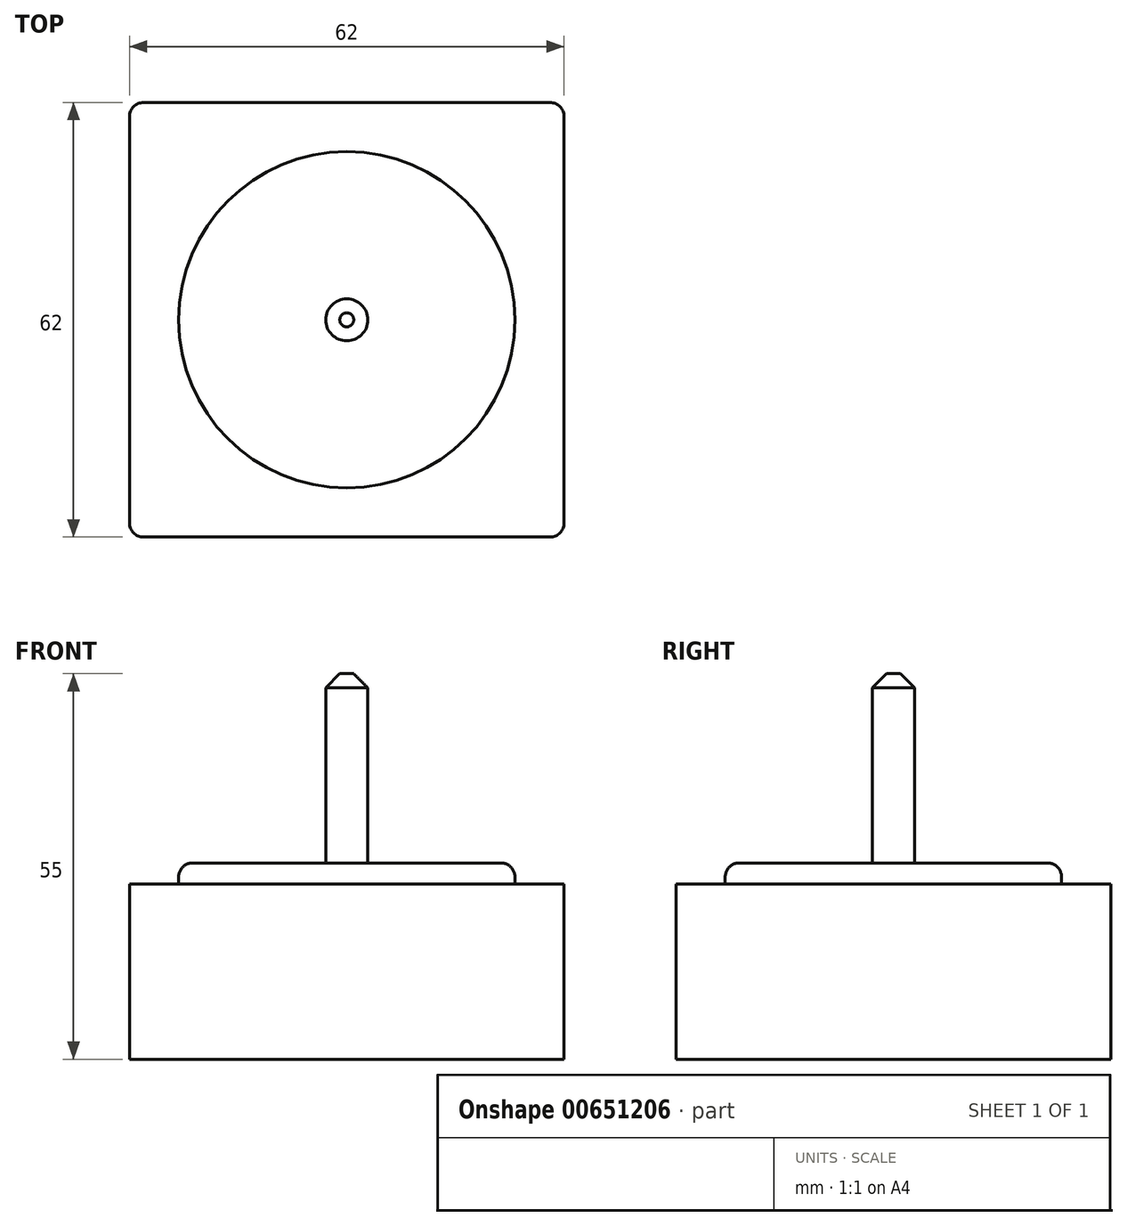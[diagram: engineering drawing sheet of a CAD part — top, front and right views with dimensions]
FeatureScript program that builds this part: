
annotation { "Feature Type Name" : "Feature", "Feature Type Description" : "" }
export const myFeature = defineFeature(function(context is Context, id is Id, definition is map)
    precondition{}
    {
        {
            var Q0;
            Q0=qCreatedBy(makeId("Top.planeOp"),FACE);
            var sketch = newSketch(context, id + "F0", { "sketchPlane" : qUnion([Q0])});
            skLineSegment(sketch, "E0.bottom", {"start": v(-31, 31) * mm, "end": v(31, 31) * mm});
            skLineSegment(sketch, "E0.top", {"start": v(-31, -31) * mm, "end": v(31, -31) * mm});
            skLineSegment(sketch, "E0.left", {"start": v(-31, 31) * mm, "end": v(-31, -31) * mm});
            skLineSegment(sketch, "E0.right", {"start": v(31, 31) * mm, "end": v(31, -31) * mm});
            skPoint(sketch, "E0.middle", {"position": v(0, 0) * mm});
            skCircle(sketch, "E1", {"center": v(0, 0) * mm, "radius": 24 * mm});
            skCircle(sketch, "E2", {"center": v(0, 0) * mm, "radius": 3 * mm});
            skSolve(sketch);
        }
        {
            var Q0;
            Q0=makeQuery(id+"F0.imprint","IMPRINT",FACE,{"disambiguationData":[TD([[makeQuery(id+"F0.imprint","IMPRINT",EDGE,{"derivedFrom":sQuery(id+"F0.wireOp",EDGE,"E1")}),1.0]])]});
            var Q1;
            Q1=makeQuery(id+"F0.imprint","IMPRINT",FACE,{"disambiguationData":[TD([[makeQuery(id+"F0.imprint","IMPRINT",EDGE,{"derivedFrom":sQuery(id+"F0.wireOp",EDGE,"E2")}),1.0]])]});
            extrude(context, id + "F1", {"entities" : qUnion([Q0, Q1]), "depth" : 3 * mm, "offsetDistance" : 25 * mm});
        }
        {
            var Q0;
            Q0=makeQuery(id+"F0.imprint","IMPRINT",FACE,{"disambiguationData":[TD([[makeQuery(id+"F0.imprint","IMPRINT",EDGE,{"derivedFrom":sQuery(id+"F0.wireOp",EDGE,"E2")}),1.0]])]});
            extrude(context, id + "F2", {"entities" : qUnion([Q0]), "operationType" : NewBodyOperationType.ADD, "depth" : 30 * mm, "offsetDistance" : 25 * mm});
        }
        {
            var Q0;
            Q0=makeQuery(id+"F0.imprint","IMPRINT",FACE,{"disambiguationData":[TD([[makeQuery(id+"F0.imprint","IMPRINT",EDGE,{"derivedFrom":sQuery(id+"F0.wireOp",EDGE,"E0.bottom")}),-1.0]])]});
            var Q1;
            Q1=makeQuery(id+"F0.imprint","IMPRINT",FACE,{"disambiguationData":[TD([[makeQuery(id+"F0.imprint","IMPRINT",EDGE,{"derivedFrom":sQuery(id+"F0.wireOp",EDGE,"E1")}),1.0]])]});
            var Q2;
            Q2=makeQuery(id+"F0.imprint","IMPRINT",FACE,{"disambiguationData":[TD([[makeQuery(id+"F0.imprint","IMPRINT",EDGE,{"derivedFrom":sQuery(id+"F0.wireOp",EDGE,"E2")}),1.0]])]});
            extrude(context, id + "F3", {"entities" : qUnion([Q0, Q1, Q2]), "operationType" : NewBodyOperationType.ADD, "oppositeDirection" : true, "depth" : 25 * mm, "offsetDistance" : 25 * mm});
        }
        {
            var Q0;
            Q0=makeQuery(id+"F3.opExtrude","SWEPT_EDGE",EDGE,{"disambiguationData":[OSD([sQuery(id+"F0.wireOp",EDGE,"E0.top"),sQuery(id+"F0.wireOp",EDGE,"E0.right")])]});
            var Q1;
            Q1=makeQuery(id+"F3.opExtrude","SWEPT_EDGE",EDGE,{"disambiguationData":[OSD([sQuery(id+"F0.wireOp",EDGE,"E0.bottom"),sQuery(id+"F0.wireOp",EDGE,"E0.right")])]});
            var Q2;
            Q2=makeQuery(id+"F3.opExtrude","SWEPT_EDGE",EDGE,{"disambiguationData":[OSD([sQuery(id+"F0.wireOp",EDGE,"E0.top"),sQuery(id+"F0.wireOp",EDGE,"E0.left")])]});
            var Q3;
            Q3=makeQuery(id+"F3.opExtrude","SWEPT_EDGE",EDGE,{"disambiguationData":[OSD([sQuery(id+"F0.wireOp",EDGE,"E0.bottom"),sQuery(id+"F0.wireOp",EDGE,"E0.left")])]});
            fillet(context, id + "F4", {"entities" : qUnion([Q0, Q1, Q2, Q3]), "tangentPropagation" : true, "radius" : 2 * mm, "defaultsChanged" : true, "vertexSettings" : [], "allowEdgeOverflow" : false});
        }
        {
            var Q0;
            Q0=makeQuery(id+"F1.opExtrude","CAP_EDGE",EDGE,{"disambiguationData":[OSD([sQuery(id+"F0.wireOp",EDGE,"E1")])],"isStart":false});
            fillet(context, id + "F5", {"entities" : qUnion([Q0]), "tangentPropagation" : true, "radius" : 2 * mm, "defaultsChanged" : true, "vertexSettings" : [], "allowEdgeOverflow" : false});
        }
        {
            var Q0;
            Q0=makeQuery(id+"F2.opExtrude","CAP_EDGE",EDGE,{"disambiguationData":[OSD([sQuery(id+"F0.wireOp",EDGE,"E2")])],"isStart":false});
            chamfer(context, id + "F6", {"entities" : qUnion([Q0]), "width" : 2 * mm, "tangentPropagation" : true});
        }
    });
